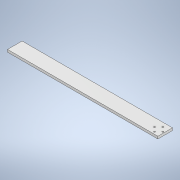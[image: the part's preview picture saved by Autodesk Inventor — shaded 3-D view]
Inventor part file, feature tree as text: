
AUTODESK INVENTOR PART (.ipt)
format: ipt  version: 2022 (Build 260153000, 153)  size: 128,512 bytes
history: native  units: mm
features: sketch x3, hole x2, other x1, extrude x1
ambient origin geometry x8: Origin, YZ Plane, XZ Plane, XY Plane, X Axis, Y Axis, Z Axis, Center Point
bodies: Body1 (feature_tree)
feature tree (7):
  other  "ソリッド1"
  extrude  "押し出し1"  Depth=30.0mm
  hole  "穴1"  [1 undecoded]
  hole  "穴3"  [1 undecoded]
  sketch  "スケッチ1"
  sketch  "スケッチ2"
  sketch  "スケッチ4"
note: 2 required parameter values undecoded (feature->parameter linkage not recoverable at this tier; creation-order binding heuristic only, values carry confidence <= 0.55)
